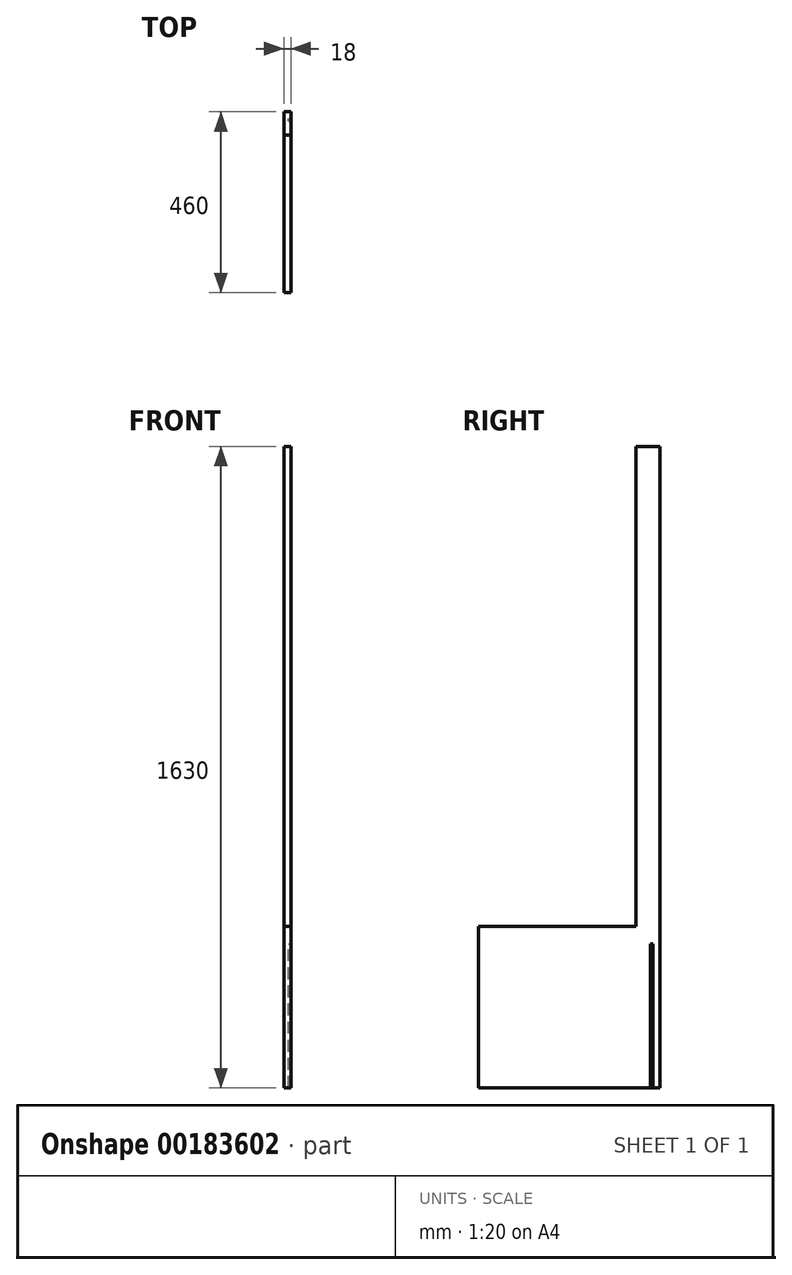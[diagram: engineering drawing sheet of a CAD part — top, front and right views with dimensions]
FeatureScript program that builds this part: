
annotation { "Feature Type Name" : "Feature", "Feature Type Description" : "" }
export const myFeature = defineFeature(function(context is Context, id is Id, definition is map)
    precondition{}
    {
        {
            var Q0;
            Q0=qCreatedBy(makeId("Right.planeOp"),FACE);
            var sketch = newSketch(context, id + "F0", { "sketchPlane" : qUnion([Q0])});
            skLineSegment(sketch, "E0.bottom", {"start": v(30, 722.5) * mm, "end": v(-30, 722.5) * mm});
            skLineSegment(sketch, "E0.left", {"start": v(30, 722.5) * mm, "end": v(30, -907.5) * mm});
            skLineSegment(sketch, "E0.right", {"start": v(-30, 722.5) * mm, "end": v(-30, -497.5) * mm});
            skPoint(sketch, "E0.middle", {"position": v(0, 0) * mm});
            skLineSegment(sketch, "E1", {"start": v(-430, -907.5) * mm, "end": v(-430, -497.5) * mm});
            skLineSegment(sketch, "E2", {"start": v(-430, -497.5) * mm, "end": v(-30, -497.5) * mm});
            skLineSegment(sketch, "E3", {"start": v(-430, -907.5) * mm, "end": v(30, -907.5) * mm});
            skSolve(sketch);
        }
        {
            var Q0;
            Q0 = qSketchRegion(id + "F0", true);
            extrude(context, id + "F1", {"entities" : qUnion([Q0]), "depth" : 18 * mm});
        }
        {
            var Q0;
            Q0=makeQuery(id+"F1.opExtrude","CAP_FACE",FACE,{"disambiguationData":[OSD([sQuery(id+"F0.wireOp",EDGE,"E0.bottom"),sQuery(id+"F0.wireOp",EDGE,"E0.left"),sQuery(id+"F0.wireOp",EDGE,"E0.right"),sQuery(id+"F0.wireOp",EDGE,"E1"),sQuery(id+"F0.wireOp",EDGE,"E2"),sQuery(id+"F0.wireOp",EDGE,"E3")])],"isStart":false});
            var sketch = newSketch(context, id + "F2", { "sketchPlane" : qUnion([Q0])});
            skLineSegment(sketch, "E4.bottom", {"start": v(12, -907.5) * mm, "end": v(6, -907.5) * mm});
            skLineSegment(sketch, "E4.top", {"start": v(12, -541.5) * mm, "end": v(6, -541.5) * mm});
            skLineSegment(sketch, "E4.left", {"start": v(12, -907.5) * mm, "end": v(12, -541.5) * mm});
            skLineSegment(sketch, "E4.right", {"start": v(6, -907.5) * mm, "end": v(6, -541.5) * mm});
            skPoint(sketch, "E4.middle", {"position": v(9, -724.5) * mm});
            skSolve(sketch);
        }
        {
            var Q0;
            Q0 = qSketchRegion(id + "F2", true);
            extrude(context, id + "F3", {"entities" : qUnion([Q0]), "operationType" : NewBodyOperationType.REMOVE, "oppositeDirection" : true, "depth" : 6 * mm});
        }
    });
